# Revit family: Emergency_Equipment-Tepid-S9300_System
name_source: partatom
category: Plumbing Fixtures
revit_build: Autodesk Revit Architecture 2016 (Build: 20150220_1215(x64)
units: mm (PartAtom-declared; Revit-internal decimal feet)

## family parameters
Always vertical = Yes
Cut with Voids When Loaded = No
OmniClass Number = 23.45.05.14
OmniClass Title = Plumbing Fixtures - Sanitary Washing Units
Part Type = Normal
Room Calculation Point = No
Round Connector Dimension = Use Diameter
Shared = No
Work Plane-Based = No

## types (6) — shared parameters
Apparent Load = 0 VA
CW Connection = Yes
Cold Water Connection = 1"
Description = Floor Mounted Tepid Emergency System
Diameter = 2' - 5"
Dimension Disclaimer = Dimensions are ±0.50”. Design and specifications are subject to change without notice.
Frequency = 60 Hz
HW Connection = No
Height = 6' - 7"
Length = 3' - 5"
Manufacturer = Stingray Systems
Model = S9300
Number of Poles = 1
Output Connection = 1"
Pipe Finish = Metal - Stingray - Copper
Power Factor = 1
Product Documentation Link = http://tepid.com
Product Name = Floor Mounted Tepid Emergency System
Product Page URL = http://tepid.com
URL = www.tepid.com
Vent Connection = No
Version = 2016-v1.0a
Waste Connection = Yes

## per-type parameters (varying)
| type | Voltage |
| 115V AC - 1.75 KW - 60 HZ - NEMA 1 | 115 V |
| 208V AC/230V AC - 1.75 KW/2.1 KW - 60 HZ - NEMA 1 | 208 V |
| 115V AC - 1.75 KW - 60 HZ - NEMA 4 | 115 V |
| 115V AC - 1.75 KW - 60 HZ - NEMA 7 | 115 V |
| 208V AC/230V AC - 1.75 KW/2.1 KW - 60 HZ - NEMA 4 | 208 V |
| 208V AC/230V AC - 1.75 KW/2.1 KW - 60 HZ - NEMA 7 | 208 V |

## geometry (parser evidence)
native form markers: Sweep x3
no freeform markers — native parametric forms only
